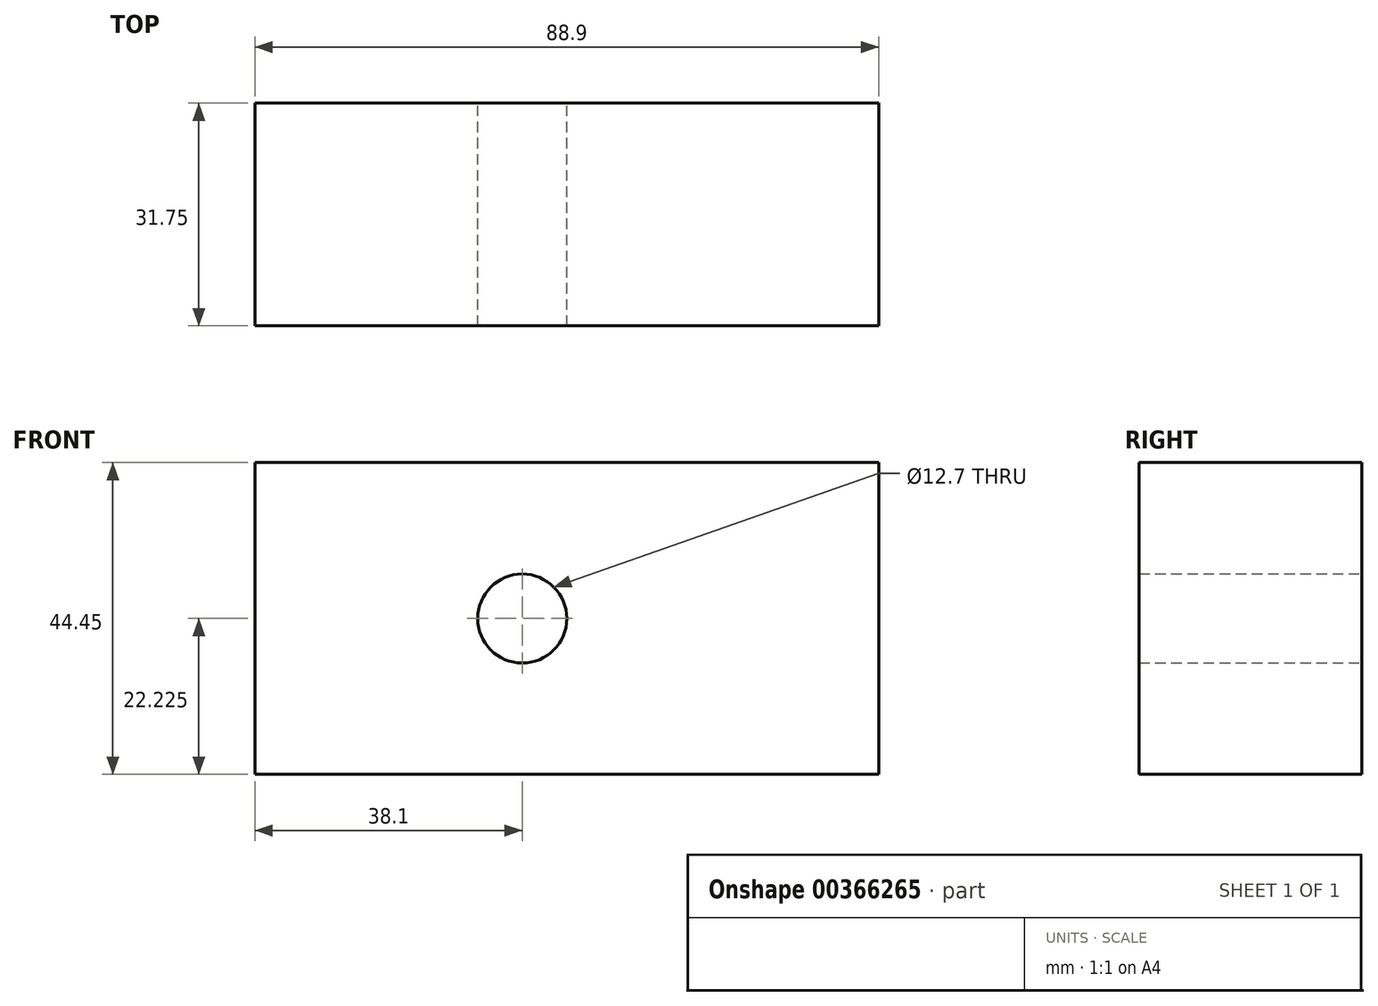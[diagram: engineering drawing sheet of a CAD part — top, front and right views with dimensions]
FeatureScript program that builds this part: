
annotation { "Feature Type Name" : "Feature", "Feature Type Description" : "" }
export const myFeature = defineFeature(function(context is Context, id is Id, definition is map)
    precondition{}
    {
        {
            var Q0;
            Q0=qCreatedBy(makeId("Front.planeOp"),FACE);
            var sketch = newSketch(context, id + "F0", { "sketchPlane" : qUnion([Q0])});
            skLineSegment(sketch, "E0", {"start": v(0, 0) * mm, "end": v(88.9, 0) * mm});
            skLineSegment(sketch, "E1", {"start": v(88.9, 0) * mm, "end": v(88.9, 44.45) * mm});
            skLineSegment(sketch, "E2", {"start": v(88.9, 44.45) * mm, "end": v(0, 44.45) * mm});
            skLineSegment(sketch, "E3", {"start": v(0, 44.45) * mm, "end": v(0, 0) * mm});
            skCircle(sketch, "E4", {"center": v(38.1, 22.23) * mm, "radius": 6.35 * mm});
            skSolve(sketch);
        }
        {
            var Q0;
            Q0=makeQuery(id+"F0.imprint","IMPRINT",FACE,{"disambiguationData":[TD([[makeQuery(id+"F0.imprint","IMPRINT",EDGE,{"derivedFrom":sQuery(id+"F0.wireOp",EDGE,"E0")}),1.0]])]});
            extrude(context, id + "F1", {"entities" : qUnion([Q0]), "depth" : 31.75 * mm});
        }
    });
